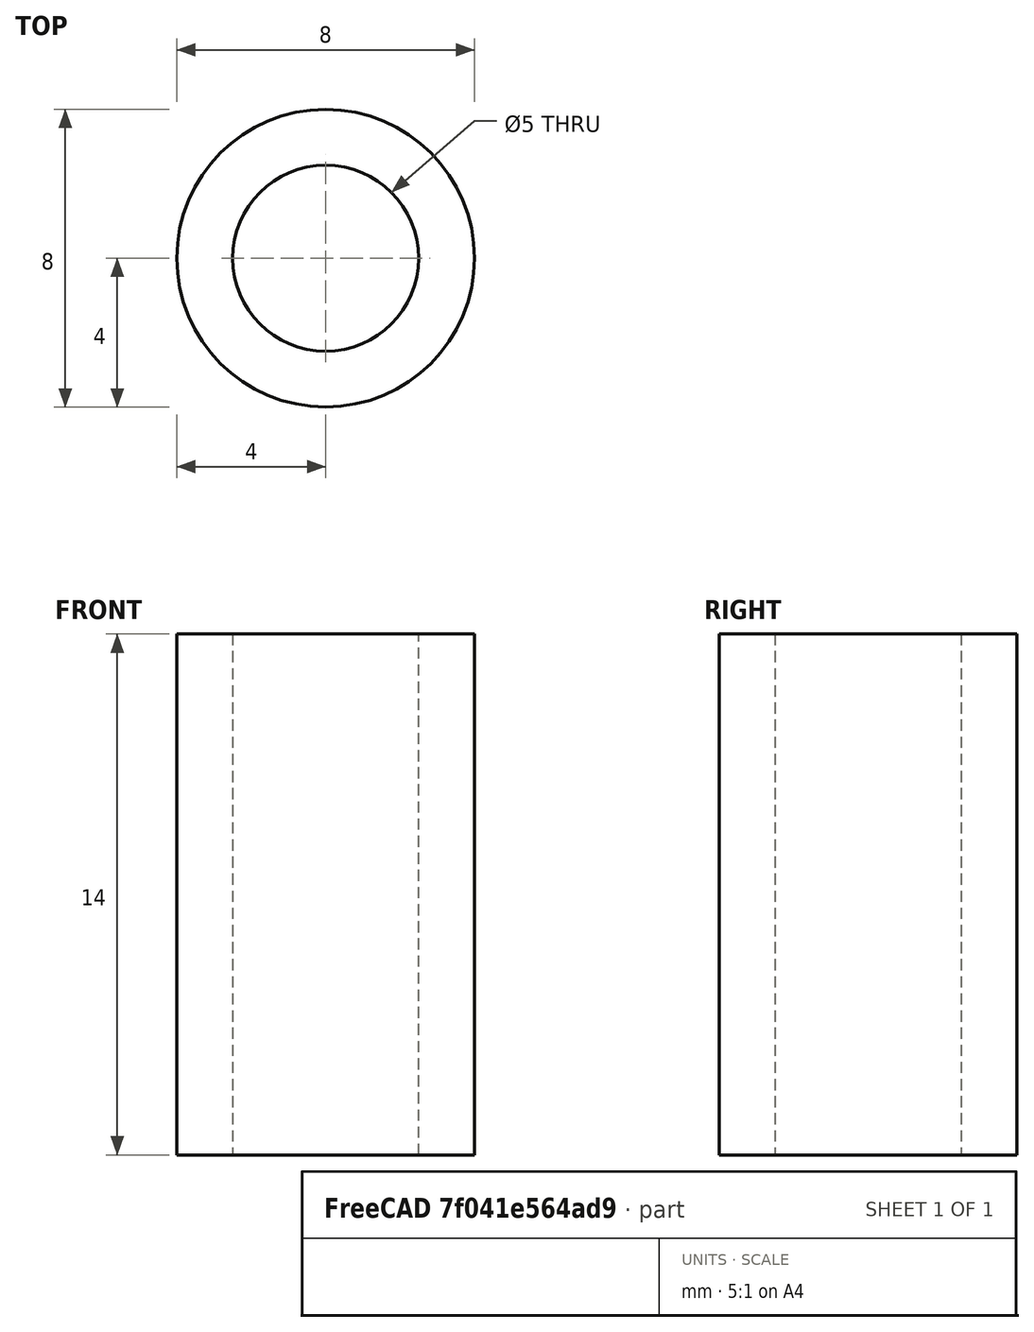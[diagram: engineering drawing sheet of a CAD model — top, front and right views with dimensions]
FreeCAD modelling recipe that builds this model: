
FCSTD DOCUMENT  (FreeCAD 0.19R24276 (Git))
Label: Rolik_6__part_1_in_print
License: All rights reserved
LicenseURL: http://en.wikipedia.org/wiki/All_rights_reserved
objects: Sketcher::SketchObject×1, PartDesign::Pad×1, PartDesign::Body×1
note: 4 computed .brp shape members not serialized (recipe doc carries the construction recipe); baked Part::Feature solids carry a one-line shape summary decoded from their .brp

FEATURE [Sketcher::SketchObject] Sketch
  FullyConstrained = true
  MapMode = 5
  Support = -> [XY_Plane]
  sketch-geometry (2):
    g0: Circle CenterX=0 CenterY=0 CenterZ=0 NormalX=0 NormalY=0 NormalZ=1 AngleXU=0 Radius=2.5
    g1: Circle CenterX=0 CenterY=0 CenterZ=0 NormalX=0 NormalY=0 NormalZ=1 AngleXU=0 Radius=4
  constraints (4):
    c: Coincident(g0,g-1)
    c: Coincident(g1,g0)
    c: Diameter(g0) = 5
    c: Diameter(g1) = 8
FEATURE [PartDesign::Pad] Pad
  Direction = (1,1,1)
  Length = 14
  Length2 = 100
  Profile = -> Sketch
  Type = 0
FEATURE [PartDesign::Body] Body
  Group = -> [Sketch,Pad]
  Origin = -> Origin
  Tip = -> Pad
